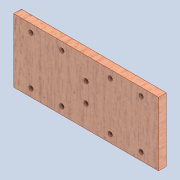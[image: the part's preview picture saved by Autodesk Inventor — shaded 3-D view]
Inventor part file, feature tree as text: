
AUTODESK INVENTOR PART (.ipt)
format: ipt  version: 2020 (Build 240168000, 168)  size: 256,512 bytes
history: native  units: mm
features: extrude x2, sketch x2
ambient origin geometry x8: Origin, YZ Plane, XZ Plane, XY Plane, X Axis, Y Axis, Z Axis, Center Point
bodies: Solid1 (feature_tree)
feature tree (4):
  extrude  "Extrusion1"  Depth=66.0mm
  extrude  "Extrusion4"  Depth=10.0mm
  sketch  "Sketch1"  dims[d0=150.0mm d1=66.0mm]
  sketch  "Sketch4"  dims[d2=8.0mm d3=0.0mm d19=4.5mm d20=18.0mm d21=8.0mm d22=8.0mm d23=32.0mm d24=18.0mm d26=32.0mm d27=0.0mm d28=0.0mm d29=10.0mm d30=10.0mm]
